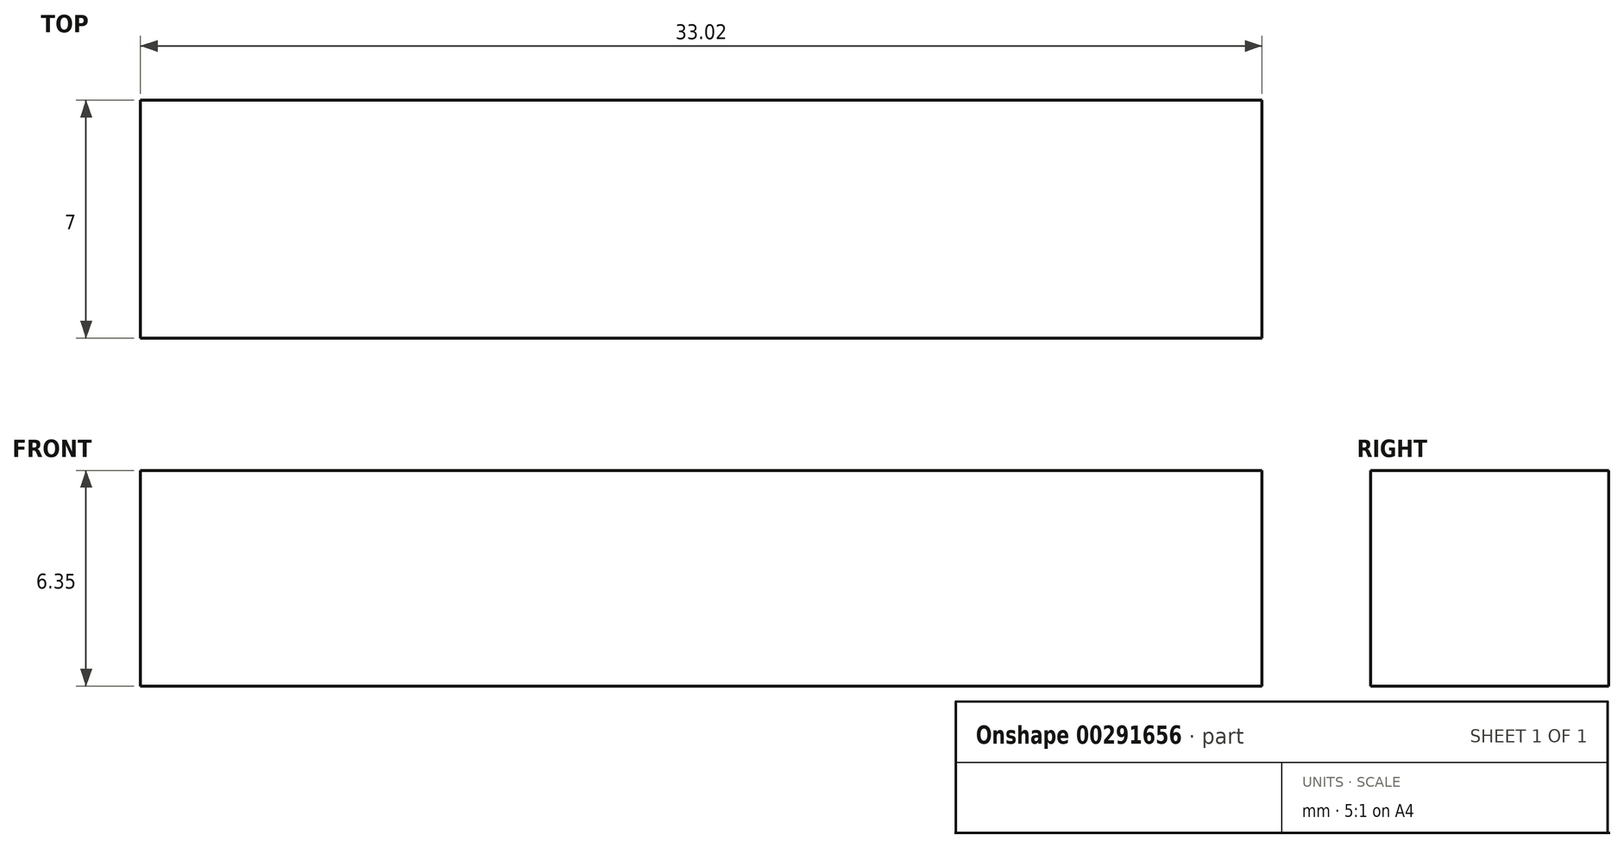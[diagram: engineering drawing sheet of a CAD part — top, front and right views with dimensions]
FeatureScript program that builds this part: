
annotation { "Feature Type Name" : "Feature", "Feature Type Description" : "" }
export const myFeature = defineFeature(function(context is Context, id is Id, definition is map)
    precondition{}
    {
        {
            var Q0;
            Q0=qCreatedBy(makeId("Front.planeOp"),FACE);
            var sketch = newSketch(context, id + "F0", { "sketchPlane" : qUnion([Q0])});
            skLineSegment(sketch, "E0.bottom", {"start": v(-26.2, 6.35) * mm, "end": v(6.83, 6.35) * mm});
            skLineSegment(sketch, "E0.top", {"start": v(-26.2, 0) * mm, "end": v(6.83, 0) * mm});
            skLineSegment(sketch, "E0.left", {"start": v(-26.2, 6.35) * mm, "end": v(-26.2, 0) * mm});
            skLineSegment(sketch, "E0.right", {"start": v(6.83, 6.35) * mm, "end": v(6.83, 0) * mm});
            skSolve(sketch);
        }
        {
            var Q0;
            Q0 = qSketchRegion(id + "F0", true);
            extrude(context, id + "F1", {"entities" : qUnion([Q0]), "endBound" : BoundingType.SYMMETRIC, "depth" : 7 * mm});
        }
    });
